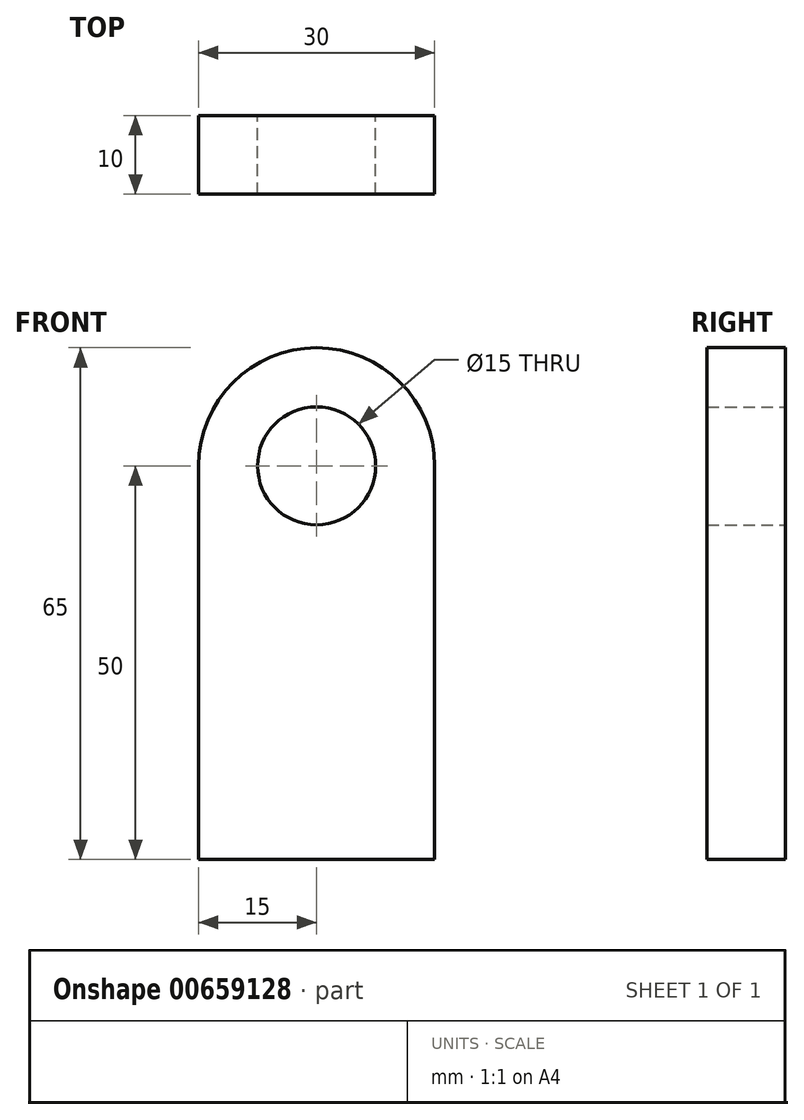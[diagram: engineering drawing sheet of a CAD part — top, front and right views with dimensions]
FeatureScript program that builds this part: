
annotation { "Feature Type Name" : "Feature", "Feature Type Description" : "" }
export const myFeature = defineFeature(function(context is Context, id is Id, definition is map)
    precondition{}
    {
        {
            var Q0;
            Q0=qCreatedBy(makeId("Front.planeOp"),FACE);
            var sketch = newSketch(context, id + "F0", { "sketchPlane" : qUnion([Q0])});
            skLineSegment(sketch, "E0", {"start": v(0, 65) * mm, "end": v(0, 0) * mm, "construction": true});
            skLineSegment(sketch, "E1", {"start": v(-15, 0) * mm, "end": v(15, 0) * mm});
            skCircle(sketch, "E2", {"center": v(0, 50) * mm, "radius": 7.5 * mm});
            skArc(sketch, "E3", {"start": v(15, 50) * mm, "mid": v(0, 65) * mm, "end": v(-15, 50) * mm});
            skLineSegment(sketch, "E4", {"start": v(-15, 50) * mm, "end": v(-15, 0) * mm});
            skLineSegment(sketch, "E5", {"start": v(15, 50) * mm, "end": v(15, 0) * mm});
            skSolve(sketch);
        }
        {
            var Q0;
            Q0 = qSketchRegion(id + "F0", true);
            extrude(context, id + "F1", {"entities" : qUnion([Q0]), "depth" : 10 * mm, "offsetDistance" : 25 * mm});
        }
    });
